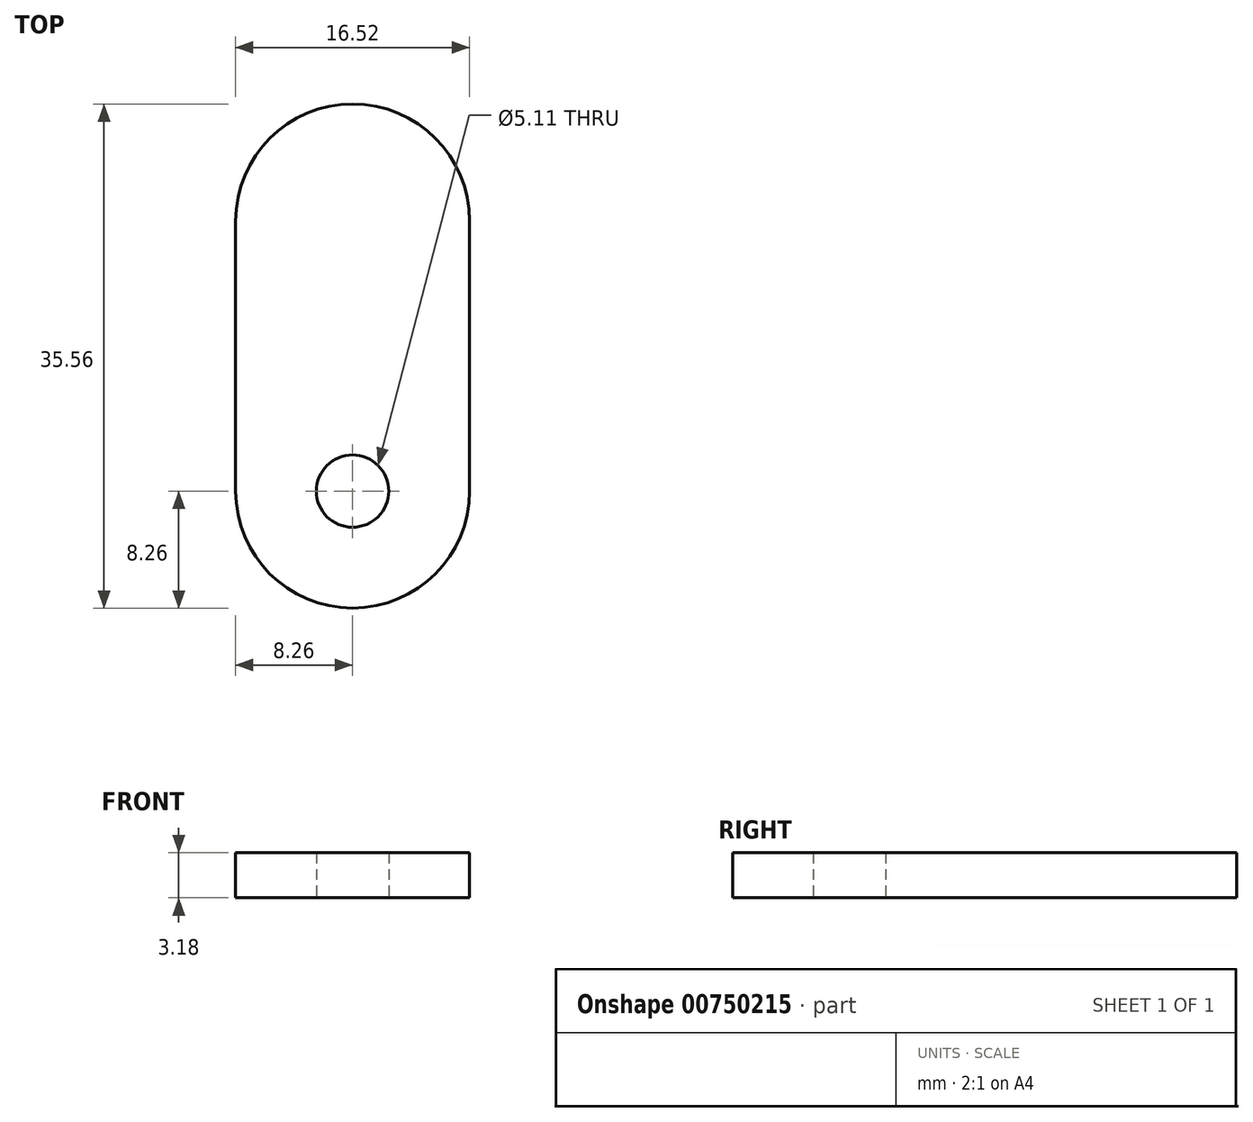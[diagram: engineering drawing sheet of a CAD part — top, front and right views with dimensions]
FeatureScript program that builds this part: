
annotation { "Feature Type Name" : "Feature", "Feature Type Description" : "" }
export const myFeature = defineFeature(function(context is Context, id is Id, definition is map)
    precondition{}
    {
        {
            var Q0;
            Q0=qCreatedBy(makeId("Top.planeOp"),FACE);
            var sketch = newSketch(context, id + "F0", { "sketchPlane" : qUnion([Q0])});
            skArc(sketch, "E0", {"start": v(-8.26, 0) * mm, "mid": v(0, -8.26) * mm, "end": v(8.26, 0) * mm});
            skCircle(sketch, "E1", {"center": v(0, 0) * mm, "radius": 2.55 * mm});
            skLineSegment(sketch, "E2", {"start": v(-8.26, 0) * mm, "end": v(-8.26, 19.05) * mm});
            skLineSegment(sketch, "E3", {"start": v(8.26, 0) * mm, "end": v(8.26, 19.05) * mm});
            skArc(sketch, "E4", {"start": v(8.26, 19.05) * mm, "mid": v(0, 27.3) * mm, "end": v(-8.26, 19.05) * mm});
            skSolve(sketch);
        }
        {
            var Q0;
            Q0 = qSketchRegion(id + "F0", true);
            extrude(context, id + "F1", {"entities" : qUnion([Q0]), "depth" : 3.17 * mm, "offsetDistance" : 25.4 * mm});
        }
    });
